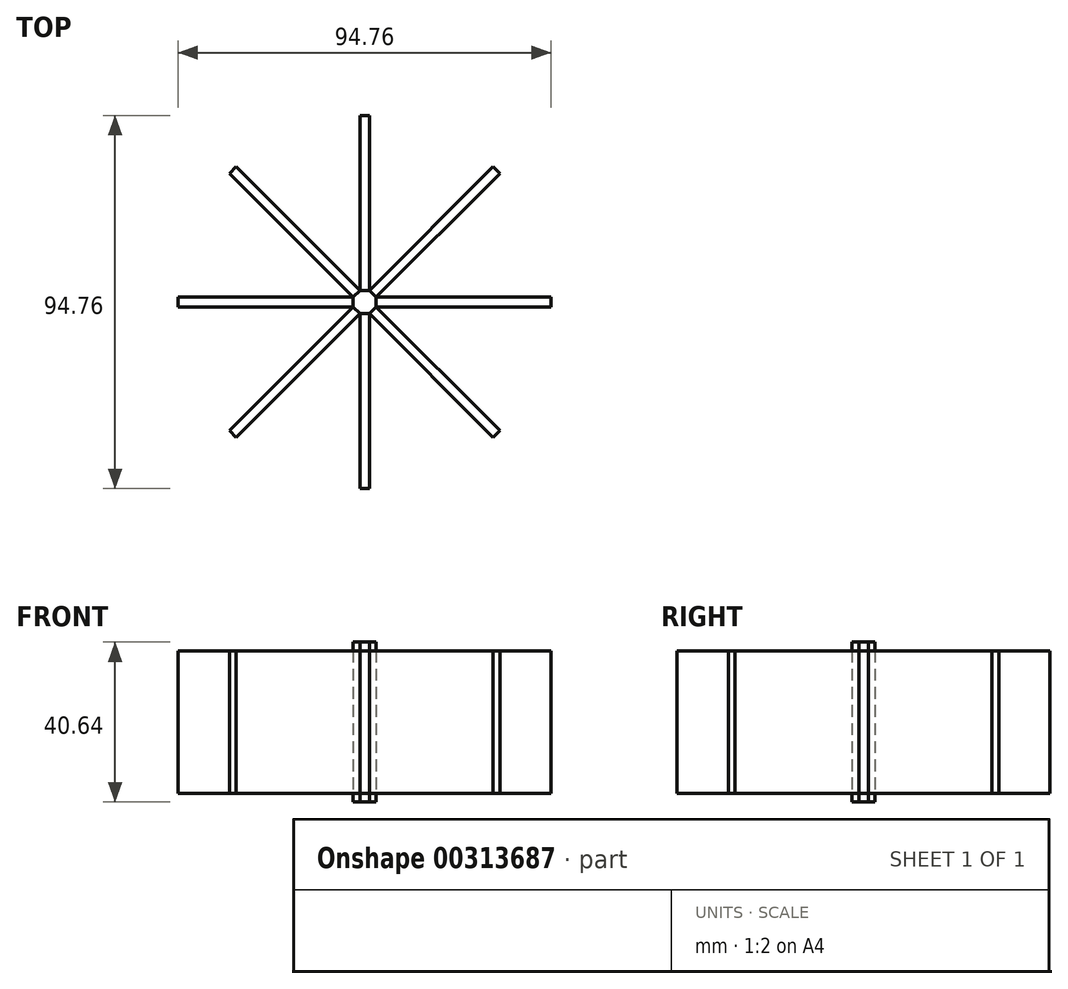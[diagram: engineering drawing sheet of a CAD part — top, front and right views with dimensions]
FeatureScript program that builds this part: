
annotation { "Feature Type Name" : "Feature", "Feature Type Description" : "" }
export const myFeature = defineFeature(function(context is Context, id is Id, definition is map)
    precondition{}
    {
        {
            var Q0;
            Q0=qCreatedBy(makeId("Top.planeOp"),FACE);
            var sketch = newSketch(context, id + "F0", { "sketchPlane" : qUnion([Q0])});
            skCircle(sketch, "E0.cCircle", {"center": v(0, 0) * mm, "radius": 3.18 * mm, "construction": true});
            skLineSegment(sketch, "E0.0", {"start": v(-1.22, 2.93) * mm, "end": v(1.22, 2.93) * mm});
            skLineSegment(sketch, "E0.1", {"start": v(1.22, 2.93) * mm, "end": v(2.93, 1.22) * mm});
            skLineSegment(sketch, "E0.2", {"start": v(2.93, 1.22) * mm, "end": v(2.93, -1.22) * mm});
            skLineSegment(sketch, "E0.3", {"start": v(2.93, -1.22) * mm, "end": v(1.22, -2.93) * mm});
            skLineSegment(sketch, "E0.4", {"start": v(1.22, -2.93) * mm, "end": v(-1.22, -2.93) * mm});
            skLineSegment(sketch, "E0.5", {"start": v(-1.22, -2.93) * mm, "end": v(-2.93, -1.22) * mm});
            skLineSegment(sketch, "E0.6", {"start": v(-2.93, -1.22) * mm, "end": v(-2.93, 1.22) * mm});
            skLineSegment(sketch, "E0.7", {"start": v(-2.93, 1.22) * mm, "end": v(-1.22, 2.93) * mm});
            skSolve(sketch);
        }
        {
            var Q0;
            Q0=makeQuery(id+"F0.imprint","IMPRINT",FACE,{"disambiguationData":[TD([[makeQuery(id+"F0.imprint","IMPRINT",EDGE,{"derivedFrom":sQuery(id+"F0.wireOp",EDGE,"E0.0")}),-1.0]])]});
            extrude(context, id + "F1", {"entities" : qUnion([Q0]), "depth" : 20.32 * mm, "hasSecondDirection" : true, "secondDirectionOppositeDirection" : true, "secondDirectionDepth" : 20.32 * mm});
        }
        {
            var Q0;
            Q0=makeQuery(id+"F1.opExtrude","SWEPT_FACE",FACE,{"disambiguationData":[OSD([sQuery(id+"F0.wireOp",EDGE,"E0.0")])]});
            var sketch = newSketch(context, id + "F2", { "sketchPlane" : qUnion([Q0])});
            skLineSegment(sketch, "E1.bottom", {"start": v(1.22, 18.1) * mm, "end": v(-1.22, 18.1) * mm});
            skLineSegment(sketch, "E1.top", {"start": v(1.22, -18.1) * mm, "end": v(-1.22, -18.1) * mm});
            skLineSegment(sketch, "E1.left", {"start": v(1.22, 18.1) * mm, "end": v(1.22, -18.1) * mm});
            skLineSegment(sketch, "E1.right", {"start": v(-1.22, 18.1) * mm, "end": v(-1.22, -18.1) * mm});
            skPoint(sketch, "E1.middle", {"position": v(0, 0) * mm});
            skSolve(sketch);
        }
        {
            var Q0;
            Q0=makeQuery(id+"F1.opExtrude","SWEPT_FACE",FACE,{"disambiguationData":[OSD([sQuery(id+"F0.wireOp",EDGE,"E0.1")])]});
            var sketch = newSketch(context, id + "F3", { "sketchPlane" : qUnion([Q0])});
            skLineSegment(sketch, "E2.bottom", {"start": v(1.22, 18.1) * mm, "end": v(-1.22, 18.1) * mm});
            skLineSegment(sketch, "E2.top", {"start": v(1.22, -18.1) * mm, "end": v(-1.22, -18.1) * mm});
            skLineSegment(sketch, "E2.left", {"start": v(1.22, 18.1) * mm, "end": v(1.22, -18.1) * mm});
            skLineSegment(sketch, "E2.right", {"start": v(-1.22, 18.1) * mm, "end": v(-1.22, -18.1) * mm});
            skPoint(sketch, "E2.middle", {"position": v(0, 0) * mm});
            skSolve(sketch);
        }
        {
            var Q0;
            Q0=makeQuery(id+"F1.opExtrude","SWEPT_FACE",FACE,{"disambiguationData":[OSD([sQuery(id+"F0.wireOp",EDGE,"E0.2")])]});
            var sketch = newSketch(context, id + "F4", { "sketchPlane" : qUnion([Q0])});
            skLineSegment(sketch, "E3.bottom", {"start": v(1.22, 18.1) * mm, "end": v(-1.22, 18.1) * mm});
            skLineSegment(sketch, "E3.top", {"start": v(1.22, -18.1) * mm, "end": v(-1.22, -18.1) * mm});
            skLineSegment(sketch, "E3.left", {"start": v(1.22, 18.1) * mm, "end": v(1.22, -18.1) * mm});
            skLineSegment(sketch, "E3.right", {"start": v(-1.22, 18.1) * mm, "end": v(-1.22, -18.1) * mm});
            skPoint(sketch, "E3.middle", {"position": v(0, 0) * mm});
            skSolve(sketch);
        }
        {
            var Q0;
            Q0=makeQuery(id+"F1.opExtrude","SWEPT_FACE",FACE,{"disambiguationData":[OSD([sQuery(id+"F0.wireOp",EDGE,"E0.3")])]});
            var sketch = newSketch(context, id + "F5", { "sketchPlane" : qUnion([Q0])});
            skLineSegment(sketch, "E4.bottom", {"start": v(1.22, 18.1) * mm, "end": v(-1.22, 18.1) * mm});
            skLineSegment(sketch, "E4.top", {"start": v(1.22, -18.1) * mm, "end": v(-1.22, -18.1) * mm});
            skLineSegment(sketch, "E4.left", {"start": v(1.22, 18.1) * mm, "end": v(1.22, -18.1) * mm});
            skLineSegment(sketch, "E4.right", {"start": v(-1.22, 18.1) * mm, "end": v(-1.22, -18.1) * mm});
            skPoint(sketch, "E4.middle", {"position": v(0, 0) * mm});
            skSolve(sketch);
        }
        {
            var Q0;
            Q0=makeQuery(id+"F1.opExtrude","SWEPT_FACE",FACE,{"disambiguationData":[OSD([sQuery(id+"F0.wireOp",EDGE,"E0.4")])]});
            var sketch = newSketch(context, id + "F6", { "sketchPlane" : qUnion([Q0])});
            skLineSegment(sketch, "E5.bottom", {"start": v(1.22, 18.1) * mm, "end": v(-1.22, 18.1) * mm});
            skLineSegment(sketch, "E5.top", {"start": v(1.22, -18.1) * mm, "end": v(-1.22, -18.1) * mm});
            skLineSegment(sketch, "E5.left", {"start": v(1.22, 18.1) * mm, "end": v(1.22, -18.1) * mm});
            skLineSegment(sketch, "E5.right", {"start": v(-1.22, 18.1) * mm, "end": v(-1.22, -18.1) * mm});
            skPoint(sketch, "E5.middle", {"position": v(0, 0) * mm});
            skSolve(sketch);
        }
        {
            var Q0;
            Q0=makeQuery(id+"F1.opExtrude","SWEPT_FACE",FACE,{"disambiguationData":[OSD([sQuery(id+"F0.wireOp",EDGE,"E0.5")])]});
            var sketch = newSketch(context, id + "F7", { "sketchPlane" : qUnion([Q0])});
            skLineSegment(sketch, "E6.bottom", {"start": v(1.22, 18.1) * mm, "end": v(-1.22, 18.1) * mm});
            skLineSegment(sketch, "E6.top", {"start": v(1.22, -18.1) * mm, "end": v(-1.22, -18.1) * mm});
            skLineSegment(sketch, "E6.left", {"start": v(1.22, 18.1) * mm, "end": v(1.22, -18.1) * mm});
            skLineSegment(sketch, "E6.right", {"start": v(-1.22, 18.1) * mm, "end": v(-1.22, -18.1) * mm});
            skPoint(sketch, "E6.middle", {"position": v(0, 0) * mm});
            skSolve(sketch);
        }
        {
            var Q0;
            Q0=makeQuery(id+"F1.opExtrude","SWEPT_FACE",FACE,{"disambiguationData":[OSD([sQuery(id+"F0.wireOp",EDGE,"E0.6")])]});
            var sketch = newSketch(context, id + "F8", { "sketchPlane" : qUnion([Q0])});
            skLineSegment(sketch, "E7.bottom", {"start": v(1.22, 18.1) * mm, "end": v(-1.22, 18.1) * mm});
            skLineSegment(sketch, "E7.top", {"start": v(1.22, -18.1) * mm, "end": v(-1.22, -18.1) * mm});
            skLineSegment(sketch, "E7.left", {"start": v(1.22, 18.1) * mm, "end": v(1.22, -18.1) * mm});
            skLineSegment(sketch, "E7.right", {"start": v(-1.22, 18.1) * mm, "end": v(-1.22, -18.1) * mm});
            skPoint(sketch, "E7.middle", {"position": v(0, 0) * mm});
            skSolve(sketch);
        }
        {
            var Q0;
            Q0=makeQuery(id+"F1.opExtrude","SWEPT_FACE",FACE,{"disambiguationData":[OSD([sQuery(id+"F0.wireOp",EDGE,"E0.7")])]});
            var sketch = newSketch(context, id + "F9", { "sketchPlane" : qUnion([Q0])});
            skLineSegment(sketch, "E8.bottom", {"start": v(1.22, 18.1) * mm, "end": v(-1.22, 18.1) * mm});
            skLineSegment(sketch, "E8.top", {"start": v(1.22, -18.1) * mm, "end": v(-1.22, -18.1) * mm});
            skLineSegment(sketch, "E8.left", {"start": v(1.22, 18.1) * mm, "end": v(1.22, -18.1) * mm});
            skLineSegment(sketch, "E8.right", {"start": v(-1.22, 18.1) * mm, "end": v(-1.22, -18.1) * mm});
            skPoint(sketch, "E8.middle", {"position": v(0, 0) * mm});
            skSolve(sketch);
        }
        {
            var Q0;
            Q0=makeQuery(id+"F2.imprint","IMPRINT",FACE,{"disambiguationData":[TD([[makeQuery(id+"F2.imprint","IMPRINT",EDGE,{"derivedFrom":sQuery(id+"F2.wireOp",EDGE,"E1.bottom")}),1.0]])]});
            extrude(context, id + "F10", {"entities" : qUnion([Q0]), "operationType" : NewBodyOperationType.ADD, "depth" : 44.45 * mm});
        }
        {
            var Q0;
            Q0=makeQuery(id+"F3.imprint","IMPRINT",FACE,{"disambiguationData":[TD([[makeQuery(id+"F3.imprint","IMPRINT",EDGE,{"derivedFrom":sQuery(id+"F3.wireOp",EDGE,"E2.bottom")}),1.0]])]});
            extrude(context, id + "F11", {"entities" : qUnion([Q0]), "operationType" : NewBodyOperationType.ADD, "depth" : 44.45 * mm});
        }
        {
            var Q0;
            Q0=makeQuery(id+"F4.imprint","IMPRINT",FACE,{"disambiguationData":[TD([[makeQuery(id+"F4.imprint","IMPRINT",EDGE,{"derivedFrom":sQuery(id+"F4.wireOp",EDGE,"E3.bottom")}),1.0]])]});
            extrude(context, id + "F12", {"entities" : qUnion([Q0]), "operationType" : NewBodyOperationType.ADD, "depth" : 44.45 * mm});
        }
        {
            var Q0;
            Q0=makeQuery(id+"F5.imprint","IMPRINT",FACE,{"disambiguationData":[TD([[makeQuery(id+"F5.imprint","IMPRINT",EDGE,{"derivedFrom":sQuery(id+"F5.wireOp",EDGE,"E4.bottom")}),1.0]])]});
            extrude(context, id + "F13", {"entities" : qUnion([Q0]), "operationType" : NewBodyOperationType.ADD, "depth" : 44.45 * mm});
        }
        {
            var Q0;
            Q0=makeQuery(id+"F6.imprint","IMPRINT",FACE,{"disambiguationData":[TD([[makeQuery(id+"F6.imprint","IMPRINT",EDGE,{"derivedFrom":sQuery(id+"F6.wireOp",EDGE,"E5.bottom")}),1.0]])]});
            extrude(context, id + "F14", {"entities" : qUnion([Q0]), "operationType" : NewBodyOperationType.ADD, "depth" : 44.45 * mm});
        }
        {
            var Q0;
            Q0=makeQuery(id+"F9.imprint","IMPRINT",FACE,{"disambiguationData":[TD([[makeQuery(id+"F9.imprint","IMPRINT",EDGE,{"derivedFrom":sQuery(id+"F9.wireOp",EDGE,"E8.bottom")}),1.0]])]});
            extrude(context, id + "F15", {"entities" : qUnion([Q0]), "operationType" : NewBodyOperationType.ADD, "depth" : 44.45 * mm});
        }
        {
            var Q0;
            Q0=makeQuery(id+"F8.imprint","IMPRINT",FACE,{"disambiguationData":[TD([[makeQuery(id+"F8.imprint","IMPRINT",EDGE,{"derivedFrom":sQuery(id+"F8.wireOp",EDGE,"E7.bottom")}),1.0]])]});
            extrude(context, id + "F16", {"entities" : qUnion([Q0]), "operationType" : NewBodyOperationType.ADD, "depth" : 44.45 * mm});
        }
        {
            var Q0;
            Q0=makeQuery(id+"F7.imprint","IMPRINT",FACE,{"disambiguationData":[TD([[makeQuery(id+"F7.imprint","IMPRINT",EDGE,{"derivedFrom":sQuery(id+"F7.wireOp",EDGE,"E6.bottom")}),1.0]])]});
            extrude(context, id + "F17", {"entities" : qUnion([Q0]), "operationType" : NewBodyOperationType.ADD, "depth" : 44.45 * mm});
        }
    });
